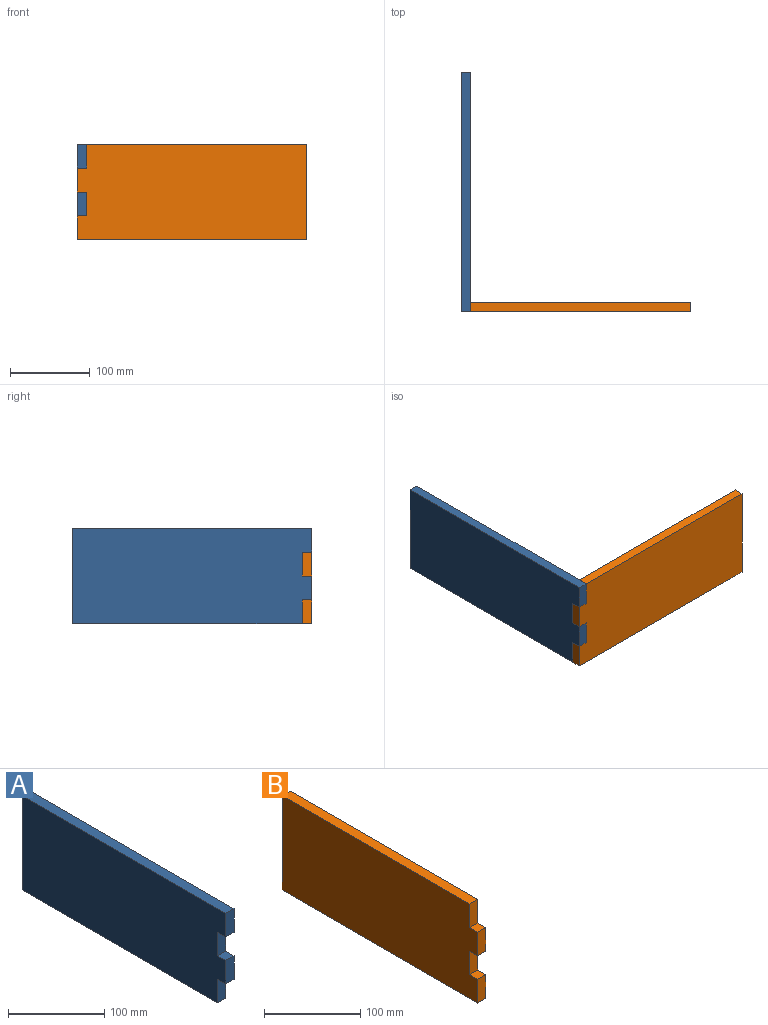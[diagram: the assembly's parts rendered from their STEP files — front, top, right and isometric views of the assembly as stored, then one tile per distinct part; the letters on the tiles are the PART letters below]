
ASSEMBLY  parts=2 mates=1
PART A: 12 faces, bbox 12x300x120 mm
  f0: plane 30x12mm, normal (0,-1,0), area 360mm2, adj f2,f3,f4,f7
  f1: plane 30x12mm, normal (0,-1,0), area 360mm2, adj f2,f3,f8,f10
  f2: plane 300x120mm, normal (-1,0,0), area 35280mm2, adj f0,f1,f4,f5,f6,f7,f8,f9
  f3: plane 300x120mm, normal (1,0,0), area 35280mm2, adj f0,f1,f4,f5,f6,f7,f8,f9
  f4: plane 300x12mm, normal (0,0,1), area 3600mm2, adj f0,f2,f3,f6
  f5: plane 288x12mm, normal (0,0,-1), area 3456mm2, adj f2,f3,f6,f11
  f6: plane 120x12mm, normal (0,1,0), area 1440mm2, adj f2,f3,f4,f5
  f7: plane 12x12mm, normal (0,0,-1), area 144mm2, adj f0,f2,f3,f9
  f8: plane 12x12mm, normal (0,0,1), area 144mm2, adj f1,f2,f3,f9
  f9: plane 30x12mm, normal (0,-1,0), area 360mm2, adj f2,f3,f7,f8
  f10: plane 12x12mm, normal (0,0,-1), area 144mm2, adj f1,f2,f3,f11
  f11: plane 30x12mm, normal (0,-1,0), area 360mm2, adj f2,f3,f5,f10
PART B: 16 faces, bbox 12x288x120 mm
  f0: plane 30x12mm, normal (0,-1,0), area 360mm2, adj f1,f6,f9,f10
  f1: plane 288x120mm, normal (-1,0,0), area 33840mm2, adj f0,f2,f3,f4,f5,f7,f8,f9
  f2: plane 276x12mm, normal (0,0,1), area 3312mm2, adj f1,f5,f6,f11
  f3: plane 30x12mm, normal (0,-1,0), area 360mm2, adj f1,f4,f6,f7
  f4: plane 288x12mm, normal (0,0,-1), area 3456mm2, adj f1,f3,f5,f6
  f5: plane 120x12mm, normal (0,1,0), area 1383.5mm2, adj f1,f2,f4,f6,f12,f14
  f6: plane 288x120mm, normal (1,0,0), area 33840mm2, adj f0,f2,f3,f4,f5,f7,f8,f9
  f7: plane 12x12mm, normal (0,0,1), area 144mm2, adj f1,f3,f6,f8
  f8: plane 30x12mm, normal (0,-1,0), area 360mm2, adj f1,f6,f7,f9
  f9: plane 12x12mm, normal (0,0,-1), area 144mm2, adj f0,f1,f6,f8
  f10: plane 12x12mm, normal (0,0,1), area 144mm2, adj f0,f1,f6,f11
  f11: plane 30x12mm, normal (0,-1,0), area 360mm2, adj f1,f2,f6,f10
  f12: cylinder r=3mm len=15mm, axis (0,1,0), area 282.7mm2, adj f5,f13
  f13: plane 6x6mm, normal (0,1,0), area 28.3mm2, adj f12
  f14: cylinder r=3mm len=15mm, axis (0,1,0), area 282.7mm2, adj f5,f15
  f15: plane 6x6mm, normal (0,1,0), area 28.3mm2, adj f14
PLACE A at identity fixed
PLACE B rot(axis=(0,0,-1),90deg) t=(138,-150,0)mm
MATE planar B.f11 <-> A.f3  axis (-1,0,0) through (0,-150,45)mm
